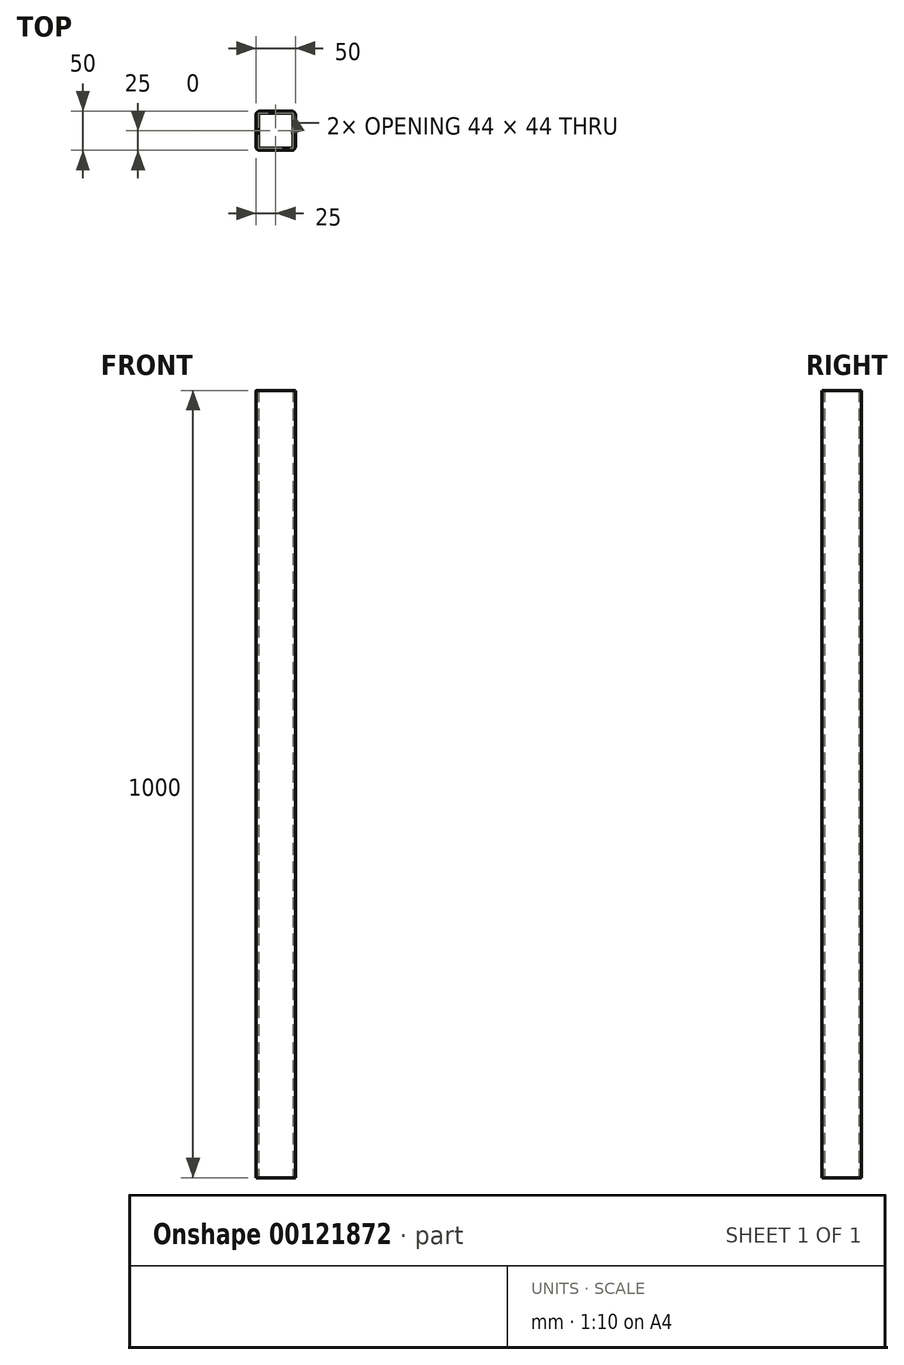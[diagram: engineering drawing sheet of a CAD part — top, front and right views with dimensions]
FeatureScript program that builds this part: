
annotation { "Feature Type Name" : "Feature", "Feature Type Description" : "" }
export const myFeature = defineFeature(function(context is Context, id is Id, definition is map)
    precondition{}
    {
        {
            var Q0;
            Q0=qCreatedBy(makeId("Top.planeOp"),FACE);
            var sketch = newSketch(context, id + "F0", { "sketchPlane" : qUnion([Q0])});
            skLineSegment(sketch, "E0.bottom", {"start": v(20, 25) * mm, "end": v(-20, 25) * mm});
            skLineSegment(sketch, "E0.top", {"start": v(20, -25) * mm, "end": v(-20, -25) * mm});
            skLineSegment(sketch, "E0.left", {"start": v(25, 20) * mm, "end": v(25, -20) * mm});
            skLineSegment(sketch, "E0.right", {"start": v(-25, 20) * mm, "end": v(-25, -20) * mm});
            skPoint(sketch, "E0.middle", {"position": v(0, 0) * mm});
            skPoint(sketch, "E1.visualSharp", {"position": v(-25, 25) * mm});
            skArc(sketch, "E1.filletArc", {"start": v(-20, 25) * mm, "mid": v(-23.54, 23.54) * mm, "end": v(-25, 20) * mm});
            skPoint(sketch, "E2.visualSharp", {"position": v(25, 25) * mm});
            skArc(sketch, "E2.filletArc", {"start": v(25, 20) * mm, "mid": v(23.54, 23.54) * mm, "end": v(20, 25) * mm});
            skPoint(sketch, "E3.visualSharp", {"position": v(-25, -25) * mm});
            skArc(sketch, "E3.filletArc", {"start": v(-25, -20) * mm, "mid": v(-23.54, -23.54) * mm, "end": v(-20, -25) * mm});
            skPoint(sketch, "E4.visualSharp", {"position": v(25, -25) * mm});
            skArc(sketch, "E4.filletArc", {"start": v(20, -25) * mm, "mid": v(23.54, -23.54) * mm, "end": v(25, -20) * mm});
            skLineSegment(sketch, "E5.0", {"start": v(20, 22) * mm, "end": v(-20, 22) * mm});
            skLineSegment(sketch, "E5.1", {"start": v(22, 20) * mm, "end": v(22, -20) * mm});
            skLineSegment(sketch, "E5.2", {"start": v(20, -22) * mm, "end": v(-20, -22) * mm});
            skLineSegment(sketch, "E5.3", {"start": v(-22, 20) * mm, "end": v(-22, -20) * mm});
            skPoint(sketch, "E6.visualSharp", {"position": v(-22, 22) * mm});
            skArc(sketch, "E6.filletArc", {"start": v(-20, 22) * mm, "mid": v(-21.41, 21.41) * mm, "end": v(-22, 20) * mm});
            skPoint(sketch, "E7.visualSharp", {"position": v(22, 22) * mm});
            skArc(sketch, "E7.filletArc", {"start": v(22, 20) * mm, "mid": v(21.41, 21.41) * mm, "end": v(20, 22) * mm});
            skPoint(sketch, "E8.visualSharp", {"position": v(22, -22) * mm});
            skArc(sketch, "E8.filletArc", {"start": v(20, -22) * mm, "mid": v(21.41, -21.41) * mm, "end": v(22, -20) * mm});
            skPoint(sketch, "E9.visualSharp", {"position": v(-22, -22) * mm});
            skArc(sketch, "E9.filletArc", {"start": v(-22, -20) * mm, "mid": v(-21.41, -21.41) * mm, "end": v(-20, -22) * mm});
            skSolve(sketch);
        }
        {
            var Q0;
            Q0 = qSketchRegion(id + "F0", true);
            extrude(context, id + "F1", {"entities" : qUnion([Q0]), "depth" : 1000 * mm});
        }
    });
